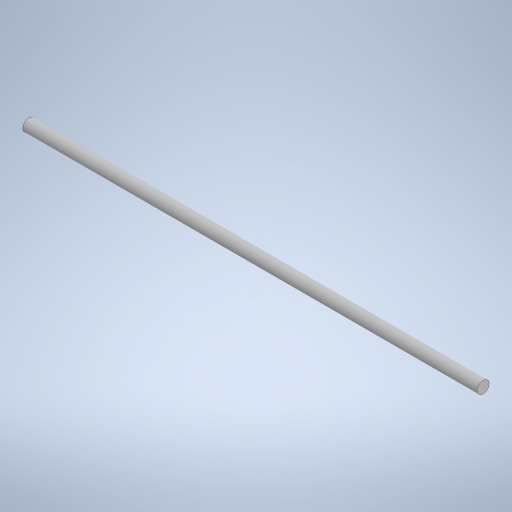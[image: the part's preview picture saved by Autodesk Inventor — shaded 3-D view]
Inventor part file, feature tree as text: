
AUTODESK INVENTOR PART (.ipt)
format: ipt  version: 2024 (Build 280153000, 153)  size: 233,984 bytes
history: native  units: in
note: dims shown in document units (in); Inventor stores cm internally (conversion verified against a paired STEP export)
features: extrude x1, sketch x1
ambient origin geometry x8: Origin, YZ Plane, XZ Plane, XY Plane, X Axis, Y Axis, Z Axis, Center Point
bodies: Solid1 (feature_tree)
feature tree (2):
  extrude  "Extrusion1"  Depth=11.75in TaperAngle=0.0deg
  sketch  "Sketch1"  dims[d0=0.315in d1=11.75in d2=0.0in]
